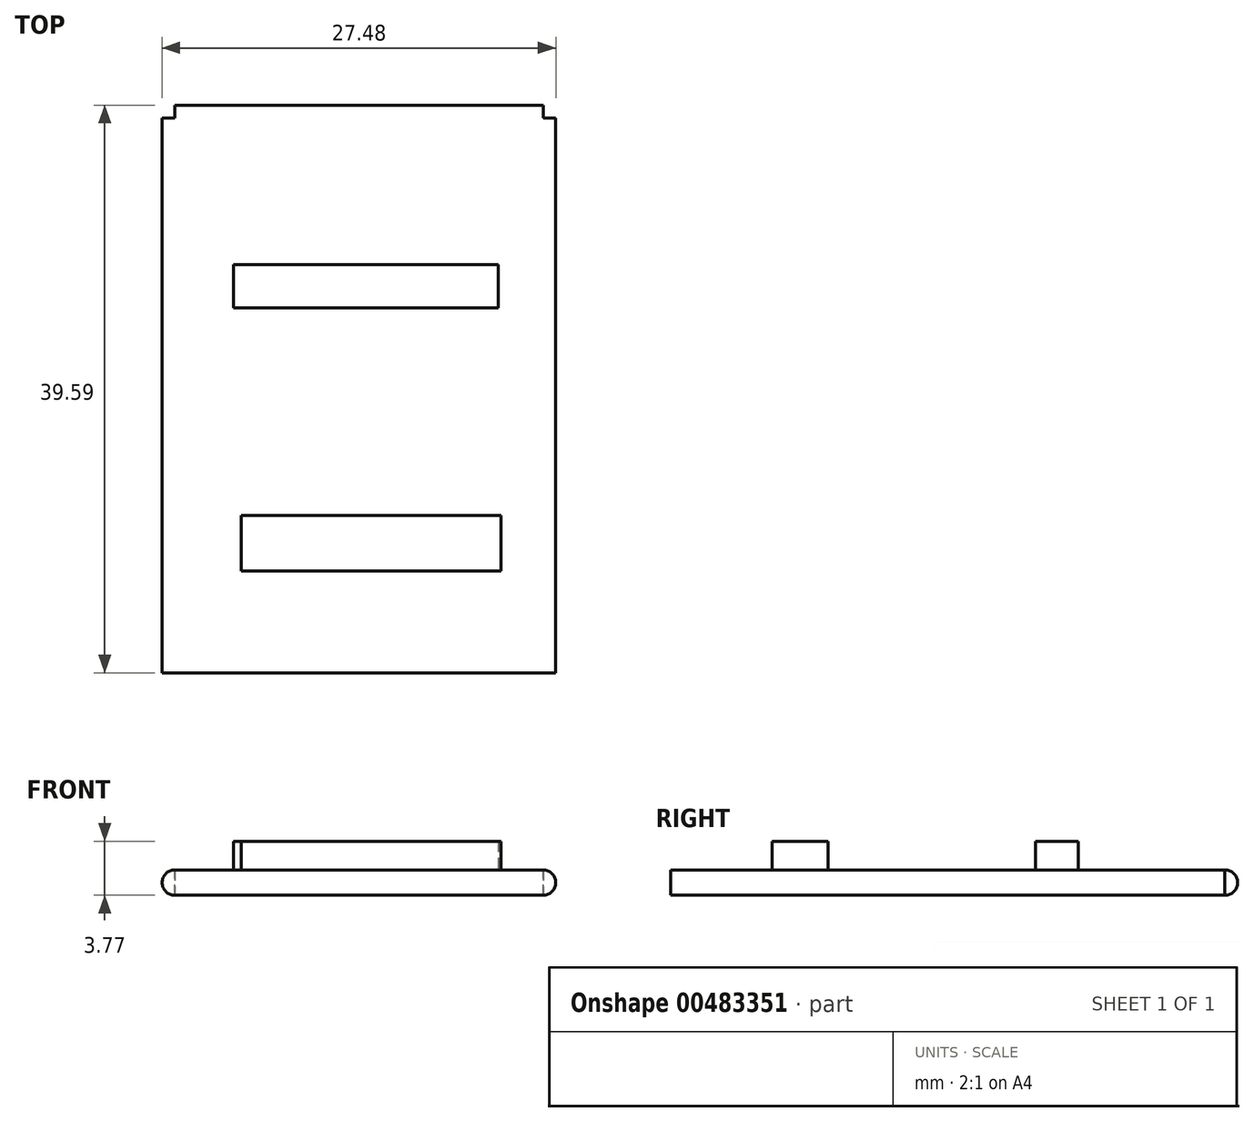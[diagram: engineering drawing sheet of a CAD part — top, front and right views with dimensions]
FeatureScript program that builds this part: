
annotation { "Feature Type Name" : "Feature", "Feature Type Description" : "" }
export const myFeature = defineFeature(function(context is Context, id is Id, definition is map)
    precondition{}
    {
        {
            var Q0;
            Q0=qCreatedBy(makeId("Top.planeOp"),FACE);
            var sketch = newSketch(context, id + "F0", { "sketchPlane" : qUnion([Q0])});
            skLineSegment(sketch, "E0.bottom", {"start": v(0, 0) * mm, "end": v(25.7, 0) * mm});
            skLineSegment(sketch, "E0.top", {"start": v(0, -38.7) * mm, "end": v(25.7, -38.7) * mm});
            skLineSegment(sketch, "E0.left", {"start": v(0, 0) * mm, "end": v(0, -38.7) * mm});
            skLineSegment(sketch, "E0.right", {"start": v(25.7, 0) * mm, "end": v(25.7, -38.7) * mm});
            skSolve(sketch);
        }
        {
            var Q0;
            Q0=makeQuery(id+"F0.imprint","IMPRINT",FACE,{"disambiguationData":[TD([[makeQuery(id+"F0.imprint","IMPRINT",EDGE,{"derivedFrom":sQuery(id+"F0.wireOp",EDGE,"E0.bottom")}),-1.0]])]});
            extrude(context, id + "F1", {"entities" : qUnion([Q0]), "depth" : 1.77 * mm});
        }
        {
            var Q0;
            Q0=makeQuery(id+"F1.opExtrude","SWEPT_FACE",FACE,{"disambiguationData":[OSD([sQuery(id+"F0.wireOp",EDGE,"E0.top")])]});
            var sketch = newSketch(context, id + "F2", { "sketchPlane" : qUnion([Q0])});
            skCircle(sketch, "E1", {"center": v(25.7, 0.89) * mm, "radius": 0.89 * mm});
            skCircle(sketch, "E2", {"center": v(0, 0.89) * mm, "radius": 0.89 * mm});
            skSolve(sketch);
        }
        {
            var Q0;
            Q0=makeQuery(id+"F1.opExtrude","SWEPT_FACE",FACE,{"disambiguationData":[OSD([sQuery(id+"F0.wireOp",EDGE,"E0.right")])]});
            var sketch = newSketch(context, id + "F3", { "sketchPlane" : qUnion([Q0])});
            skCircle(sketch, "E3", {"center": v(0, 0.89) * mm, "radius": 0.89 * mm});
            skSolve(sketch);
        }
        {
            var Q0;
            {var subQ1=sQuery(id+"F0.wireOp",EDGE,"E0.top");var subQ2=makeQuery(id+"F1.opExtrude","SWEPT_EDGE",EDGE,{"disambiguationData":[OSD([subQ1,sQuery(id+"F0.wireOp",EDGE,"E0.right")])]});Q0=makeQuery(id+"F2.imprint","IMPRINT",FACE,{"disambiguationData":[TD([[makeQuery(id+"F2.imprint","IMPRINT",EDGE,{"derivedFrom":subQ2}),1.0]])]});}
            var Q1;
            {var subQ1=sQuery(id+"F0.wireOp",EDGE,"E0.top");var subQ2=makeQuery(id+"F1.opExtrude","SWEPT_EDGE",EDGE,{"disambiguationData":[OSD([subQ1,sQuery(id+"F0.wireOp",EDGE,"E0.left")])]});Q1=makeQuery(id+"F2.imprint","IMPRINT",FACE,{"disambiguationData":[TD([[makeQuery(id+"F2.imprint","IMPRINT",EDGE,{"derivedFrom":subQ2}),-1.0]])]});}
            extrude(context, id + "F4", {"entities" : qUnion([Q0, Q1]), "operationType" : NewBodyOperationType.ADD, "oppositeDirection" : true, "depth" : 38.7 * mm});
        }
        {
            var Q0;
            {var subQ1=sQuery(id+"F0.wireOp",EDGE,"E0.right");var subQ2=makeQuery(id+"F1.opExtrude","SWEPT_EDGE",EDGE,{"disambiguationData":[OSD([sQuery(id+"F0.wireOp",EDGE,"E0.bottom"),subQ1])]});Q0=makeQuery(id+"F3.imprint","IMPRINT",FACE,{"disambiguationData":[TD([[makeQuery(id+"F3.imprint","IMPRINT",EDGE,{"derivedFrom":subQ2}),1.0]])]});}
            extrude(context, id + "F5", {"entities" : qUnion([Q0]), "operationType" : NewBodyOperationType.ADD, "oppositeDirection" : true, "depth" : 25.7 * mm});
        }
        {
            var Q0;
            Q0=makeQuery(id+"F1.opExtrude","CAP_FACE",FACE,{"disambiguationData":[OSD([sQuery(id+"F0.wireOp",EDGE,"E0.bottom"),sQuery(id+"F0.wireOp",EDGE,"E0.top"),sQuery(id+"F0.wireOp",EDGE,"E0.left"),sQuery(id+"F0.wireOp",EDGE,"E0.right")])],"isStart":false});
            var sketch = newSketch(context, id + "F6", { "sketchPlane" : qUnion([Q0])});
            skLineSegment(sketch, "E4.bottom", {"start": v(4.62, -31.6) * mm, "end": v(22.78, -31.6) * mm});
            skLineSegment(sketch, "E4.top", {"start": v(4.62, -27.71) * mm, "end": v(22.78, -27.71) * mm});
            skLineSegment(sketch, "E4.left", {"start": v(4.62, -31.6) * mm, "end": v(4.62, -27.71) * mm});
            skLineSegment(sketch, "E4.right", {"start": v(22.78, -31.6) * mm, "end": v(22.78, -27.71) * mm});
            skLineSegment(sketch, "E5.bottom", {"start": v(4.13, -23.05) * mm, "end": v(22.5, -23.05) * mm});
            skLineSegment(sketch, "E5.top", {"start": v(4.13, -20.06) * mm, "end": v(22.5, -20.06) * mm});
            skLineSegment(sketch, "E5.left", {"start": v(4.13, -23.05) * mm, "end": v(4.13, -20.06) * mm});
            skLineSegment(sketch, "E5.right", {"start": v(22.5, -23.05) * mm, "end": v(22.5, -20.06) * mm});
            skLineSegment(sketch, "E6.bottom", {"start": v(4.09, -13.24) * mm, "end": v(22.57, -13.24) * mm});
            skLineSegment(sketch, "E6.top", {"start": v(4.09, -10.24) * mm, "end": v(22.57, -10.24) * mm});
            skLineSegment(sketch, "E6.left", {"start": v(4.09, -13.24) * mm, "end": v(4.09, -10.24) * mm});
            skLineSegment(sketch, "E6.right", {"start": v(22.57, -13.24) * mm, "end": v(22.57, -10.24) * mm});
            skSolve(sketch);
        }
        {
            var Q0;
            Q0=makeQuery(id+"F6.imprint","IMPRINT",FACE,{"disambiguationData":[TD([[makeQuery(id+"F6.imprint","IMPRINT",EDGE,{"derivedFrom":sQuery(id+"F6.wireOp",EDGE,"E4.bottom")}),1.0]])]});
            var Q1;
            Q1=makeQuery(id+"F6.imprint","IMPRINT",FACE,{"disambiguationData":[TD([[makeQuery(id+"F6.imprint","IMPRINT",EDGE,{"derivedFrom":sQuery(id+"F6.wireOp",EDGE,"E6.bottom")}),1.0]])]});
            extrude(context, id + "F7", {"entities" : qUnion([Q0, Q1]), "operationType" : NewBodyOperationType.ADD, "depth" : 2 * mm});
        }
    });
